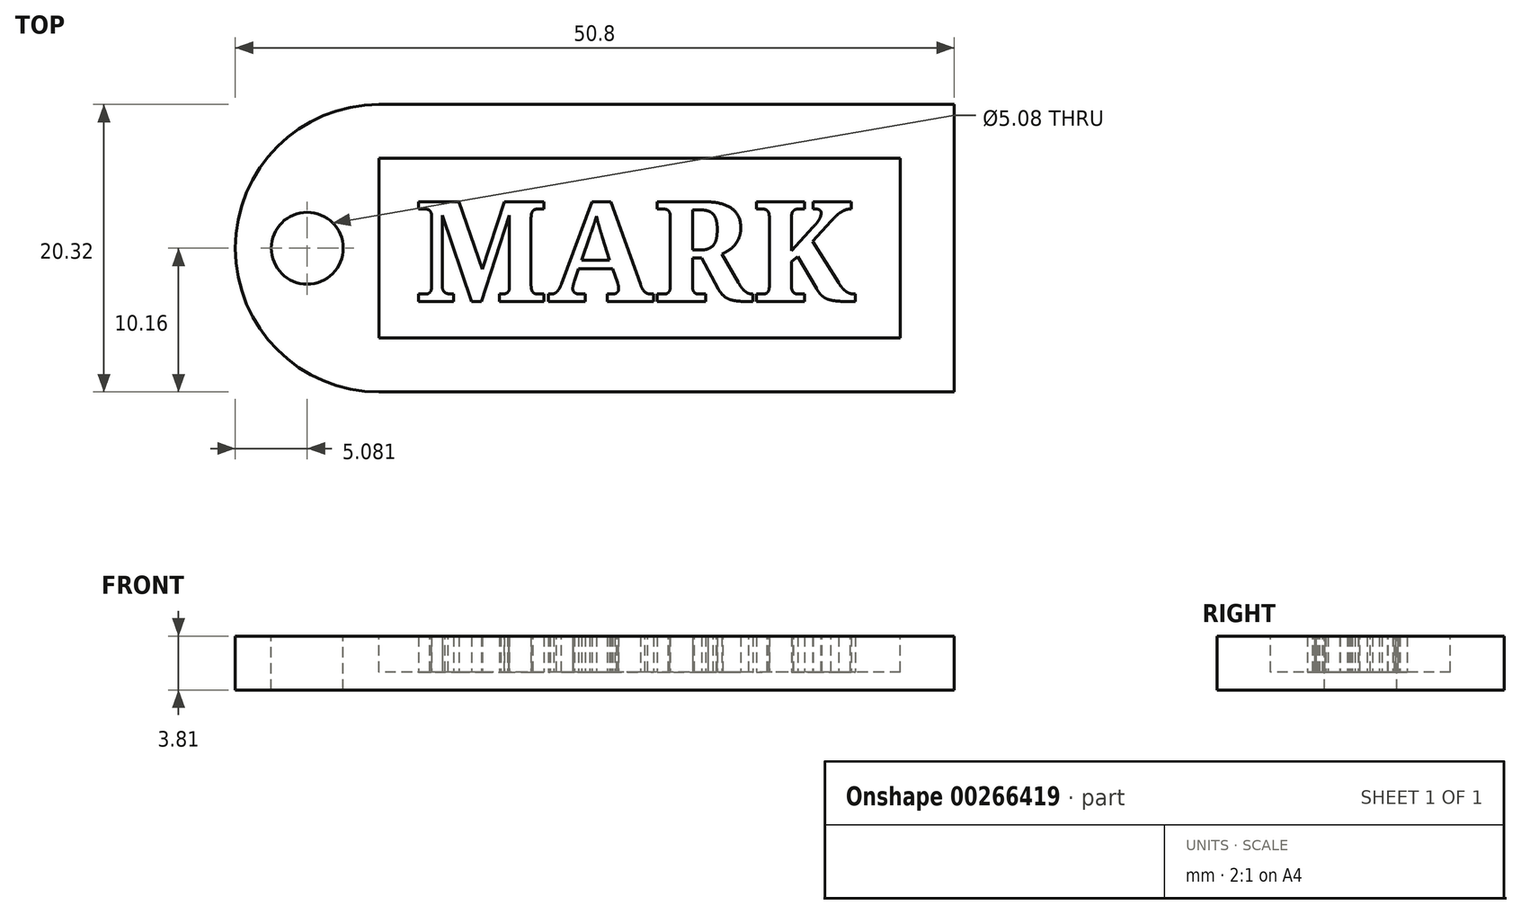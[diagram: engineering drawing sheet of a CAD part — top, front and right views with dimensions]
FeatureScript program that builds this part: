
annotation { "Feature Type Name" : "Feature", "Feature Type Description" : "" }
export const myFeature = defineFeature(function(context is Context, id is Id, definition is map)
    precondition{}
    {
        {
            var Q0;
            Q0=qCreatedBy(makeId("Top.planeOp"),FACE);
            var sketch = newSketch(context, id + "F0", { "sketchPlane" : qUnion([Q0])});
            skLineSegment(sketch, "E0.bottom", {"start": v(8.83, 37.87) * mm, "end": v(49.47, 37.87) * mm});
            skLineSegment(sketch, "E0.top", {"start": v(8.83, 17.55) * mm, "end": v(49.47, 17.55) * mm});
            skLineSegment(sketch, "E0.left", {"start": v(-1.33, 27.71) * mm, "end": v(-1.33, 27.71) * mm});
            skLineSegment(sketch, "E0.right", {"start": v(49.47, 37.87) * mm, "end": v(49.47, 17.55) * mm});
            skPoint(sketch, "E1.visualSharp", {"position": v(-1.33, 37.87) * mm});
            skArc(sketch, "E1.filletArc", {"start": v(8.83, 37.87) * mm, "mid": v(1.65, 34.9) * mm, "end": v(-1.33, 27.71) * mm});
            skPoint(sketch, "E2.visualSharp", {"position": v(-1.33, 17.55) * mm});
            skArc(sketch, "E2.filletArc", {"start": v(-1.33, 27.71) * mm, "mid": v(1.65, 20.53) * mm, "end": v(8.83, 17.55) * mm});
            skSolve(sketch);
        }
        {
            var Q0;
            Q0 = qSketchRegion(id + "F0", true);
            extrude(context, id + "F1", {"entities" : qUnion([Q0]), "depth" : 3.8 * mm});
        }
        {
            var Q0;
            Q0=makeQuery(id+"F1.opExtrude","CAP_FACE",FACE,{"disambiguationData":[OSD([sQuery(id+"F0.wireOp",EDGE,"E0.bottom"),sQuery(id+"F0.wireOp",EDGE,"E0.top"),sQuery(id+"F0.wireOp",EDGE,"E0.right"),sQuery(id+"F0.wireOp",EDGE,"E1.filletArc"),sQuery(id+"F0.wireOp",EDGE,"E2.filletArc")])],"isStart":false});
            var sketch = newSketch(context, id + "F2", { "sketchPlane" : qUnion([Q0])});
            skPoint(sketch, "E3", {"position": v(45.66, 34.06) * mm});
            skPoint(sketch, "E4", {"position": v(8.83, 21.36) * mm});
            skLineSegment(sketch, "E5.bottom", {"start": v(45.66, 34.06) * mm, "end": v(8.83, 34.06) * mm});
            skLineSegment(sketch, "E5.top", {"start": v(45.66, 21.36) * mm, "end": v(8.83, 21.36) * mm});
            skLineSegment(sketch, "E5.left", {"start": v(45.66, 34.06) * mm, "end": v(45.66, 21.36) * mm});
            skLineSegment(sketch, "E5.right", {"start": v(8.83, 34.06) * mm, "end": v(8.83, 21.36) * mm});
            skSolve(sketch);
        }
        {
            var Q0;
            Q0 = qSketchRegion(id + "F2", true);
            extrude(context, id + "F3", {"entities" : qUnion([Q0]), "operationType" : NewBodyOperationType.REMOVE, "oppositeDirection" : true, "depth" : 2.54 * mm});
        }
        {
            var Q0;
            Q0=makeQuery(id+"F1.opExtrude","CAP_FACE",FACE,{"disambiguationData":[OSD([sQuery(id+"F0.wireOp",EDGE,"E0.bottom"),sQuery(id+"F0.wireOp",EDGE,"E0.top"),sQuery(id+"F0.wireOp",EDGE,"E0.right"),sQuery(id+"F0.wireOp",EDGE,"E1.filletArc"),sQuery(id+"F0.wireOp",EDGE,"E2.filletArc")])],"isStart":false});
            var sketch = newSketch(context, id + "F4", { "sketchPlane" : qUnion([Q0])});
            skPoint(sketch, "E6", {"position": v(3.75, 27.71) * mm});
            skPoint(sketch, "E6.positionSnap0", {"position": v(-1.33, 27.71) * mm});
            skCircle(sketch, "E7", {"center": v(3.75, 27.71) * mm, "radius": 2.54 * mm});
            skSolve(sketch);
        }
        {
            var Q0;
            Q0 = qSketchRegion(id + "F4", true);
            extrude(context, id + "F5", {"entities" : qUnion([Q0]), "operationType" : NewBodyOperationType.REMOVE, "oppositeDirection" : true, "depth" : 25.4 * mm});
        }
        {
            var Q0;
            Q0=makeQuery(id+"F3.boolean.opBoolean","COPY",FACE,{"derivedFrom":makeQuery(id+"F3.opExtrude","CAP_FACE",FACE,{"disambiguationData":[OSD([sQuery(id+"F2.wireOp",EDGE,"E5.bottom"),sQuery(id+"F2.wireOp",EDGE,"E5.top"),sQuery(id+"F2.wireOp",EDGE,"E5.left"),sQuery(id+"F2.wireOp",EDGE,"E5.right")])],"isStart":false})});
            var sketch = newSketch(context, id + "F6", { "sketchPlane" : qUnion([Q0])});
            skText(sketch, "E8", { "text": "MARK\n", "fontName": "NotoSerif-Bold.ttf"});
            const initialGuessF6  = {"E8": [0.01135, 0.02394, 1, 0, 0.00712]};
            skSetInitialGuess(sketch, initialGuessF6);
            skSolve(sketch);
        }
        {
            var Q0;
            Q0 = qSketchRegion(id + "F6", true);
            extrude(context, id + "F7", {"entities" : qUnion([Q0]), "operationType" : NewBodyOperationType.ADD, "depth" : 2.54 * mm});
        }
    });
